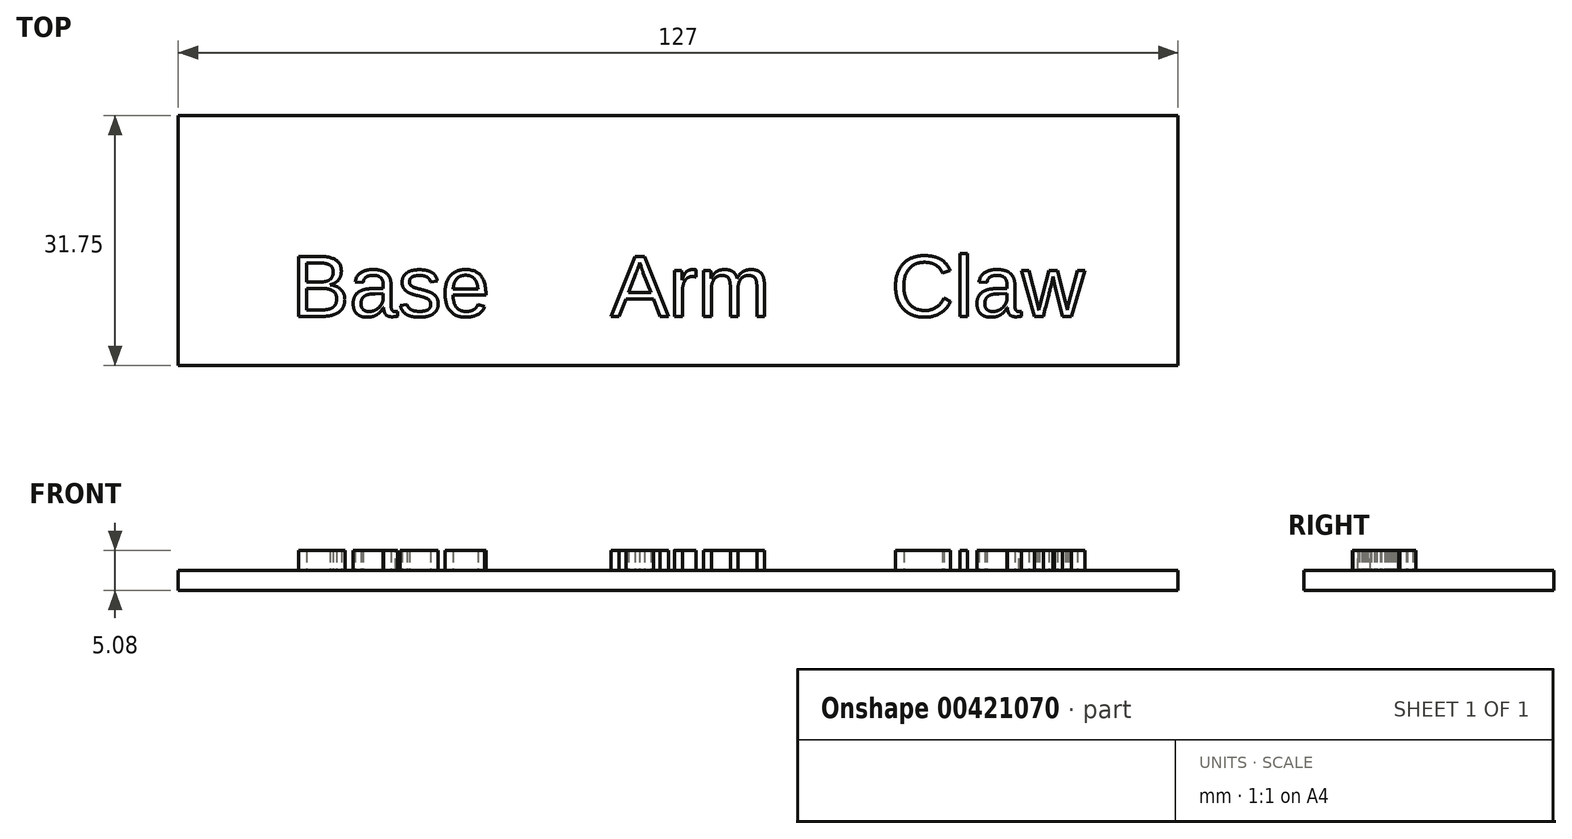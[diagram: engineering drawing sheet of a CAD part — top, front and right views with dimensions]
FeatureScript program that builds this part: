
annotation { "Feature Type Name" : "Feature", "Feature Type Description" : "" }
export const myFeature = defineFeature(function(context is Context, id is Id, definition is map)
    precondition{}
    {
        {
            var Q0;
            Q0=qCreatedBy(makeId("Top.planeOp"),FACE);
            var sketch = newSketch(context, id + "F0", { "sketchPlane" : qUnion([Q0])});
            skLineSegment(sketch, "E0.bottom", {"start": v(-64.8, 22.54) * mm, "end": v(62.2, 22.54) * mm});
            skLineSegment(sketch, "E0.top", {"start": v(-64.8, -9.21) * mm, "end": v(62.2, -9.21) * mm});
            skLineSegment(sketch, "E0.left", {"start": v(-64.8, 22.54) * mm, "end": v(-64.8, -9.21) * mm});
            skLineSegment(sketch, "E0.right", {"start": v(62.2, 22.54) * mm, "end": v(62.2, -9.21) * mm});
            skSolve(sketch);
        }
        {
            var Q0;
            Q0 = qSketchRegion(id + "F0", true);
            extrude(context, id + "F1", {"entities" : qUnion([Q0]), "depth" : 2.54 * mm});
        }
        {
            var Q0;
            Q0=makeQuery(id+"F1.opExtrude","CAP_FACE",FACE,{"disambiguationData":[OSD([sQuery(id+"F0.wireOp",EDGE,"E0.bottom"),sQuery(id+"F0.wireOp",EDGE,"E0.top"),sQuery(id+"F0.wireOp",EDGE,"E0.left"),sQuery(id+"F0.wireOp",EDGE,"E0.right")])],"isStart":false});
            var sketch = newSketch(context, id + "F2", { "sketchPlane" : qUnion([Q0])});
            skText(sketch, "E1", { "text": "Base     Arm     Claw", "fontName": "Arimo-Regular.ttf"});
            const initialGuessF2  = {"E1": [-0.05042, -0.00298, 1, 0, 0.00796]};
            skSetInitialGuess(sketch, initialGuessF2);
            skSolve(sketch);
        }
        {
            var Q0;
            Q0 = qSketchRegion(id + "F2", true);
            extrude(context, id + "F3", {"entities" : qUnion([Q0]), "operationType" : NewBodyOperationType.ADD, "depth" : 2.54 * mm});
        }
    });
